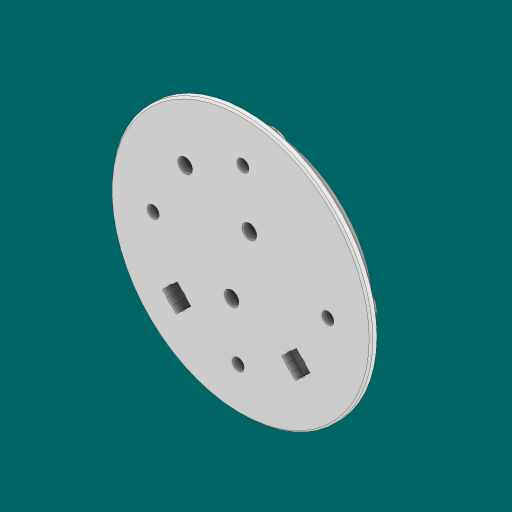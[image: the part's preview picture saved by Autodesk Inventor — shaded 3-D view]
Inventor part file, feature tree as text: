
AUTODESK INVENTOR PART (.ipt)
format: ipt  version: 2023.1 (Build 271208000, 208)  size: 1,416,192 bytes
history: native  units: in
note: dims shown in document units (in); Inventor stores cm internally (conversion verified against a paired STEP export)
features: extrude x6, sketch x6, projected_geometry x5, other x3, chamfer x2, reference x2, fillet x1
ambient origin geometry x8: Origin, YZ Plane, XZ Plane, XY Plane, X Axis, Y Axis, Z Axis, Center Point
bodies: Solid1 (feature_tree)
feature tree (25):
  extrude  "Extrusion1"  Depth=1.5748in TaperAngle=360.0deg
  extrude  "Extrusion2"  Depth=0.3in
  fillet  "Fillet1"  Radius=1.5748in
  extrude  "Extrusion4"  Depth=0.0472in
  chamfer  "Chamfer1"  Distance=0.1in
  chamfer  "Chamfer2"  Distance=0.0236in Angle=45.0deg
  extrude  "Extrusion5"  Depth=0.19in
  extrude  "Extrusion6"  Depth=0.3543in
  extrude  "Extrusion8"  Depth=0.3543in
  sketch  "Sketch1"  dims[d0=0.1562in d1=1.5748in d3=360.0deg]
  reference  "Reference1"
  reference  "Reference2"
  sketch  "Sketch2"  dims[d5=0.3in d6=0.0in d7=0.4724in d8=1.5748in d10=360.0deg]
  projected_geometry  "Projected Loop1"
  sketch  "Sketch4"  dims[d12=0.0472in d13=0.0in d14=0.25in]
  projected_geometry  "Projected Loop3"
  sketch  "Sketch5"  dims[d22=3.4in d23=0.1in d24=0.0in d25=0.0236in d26=0.125in d27=45.0deg]
  projected_geometry  "Projected Loop4"
  sketch  "Sketch6"  dims[d28=0.125in d29=0.125in d30=45.0deg d31=0.19in]
  projected_geometry  "Projected Loop5"
  sketch  "Sketch8"  dims[d32=0.1in d33=0.0in d34=0.33in d35=0.33in d36=0.33in d37=0.1in d38=0.0in d46=0.3543in d47=0.7874in d49=360.0deg d51=0.25in d52=1.0in d53=0.0in]
  projected_geometry  "Projected Loop7"
  other  "<userpath>\Documents\CAD\guardSwerve5\MainAssy.iam"
  other  "MainAssy.iam"
  other  "Carriage:1"
